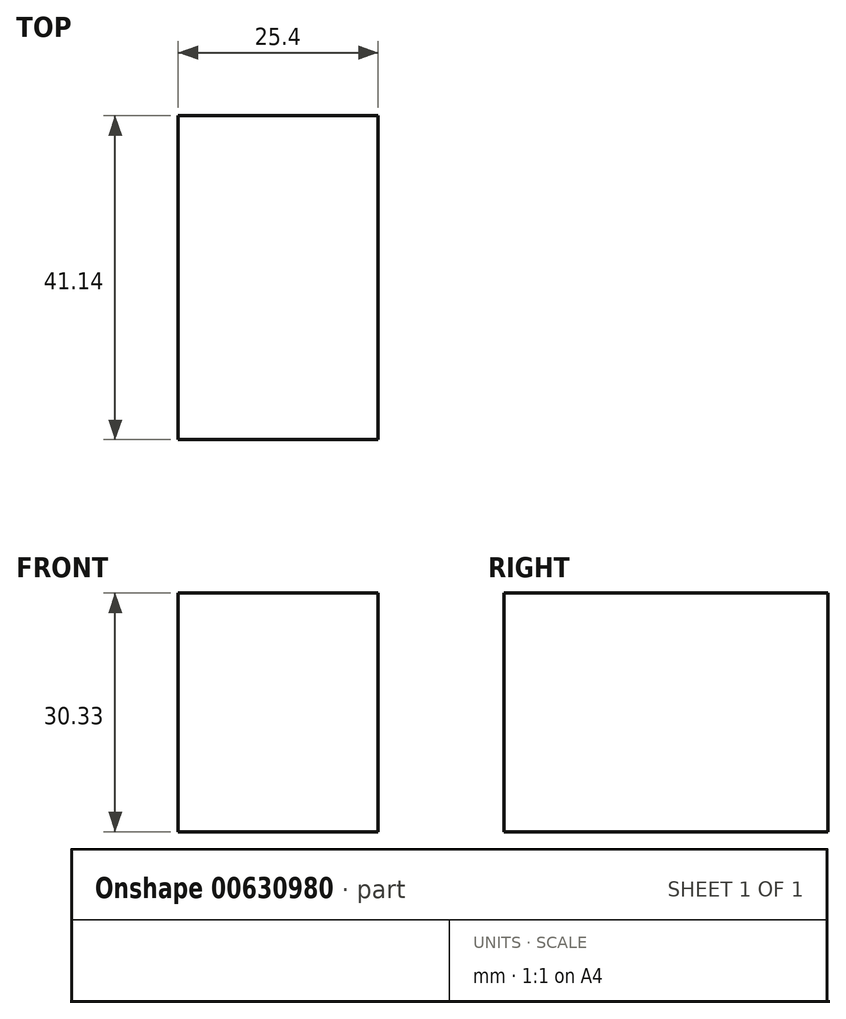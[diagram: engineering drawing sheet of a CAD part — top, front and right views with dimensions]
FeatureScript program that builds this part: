
annotation { "Feature Type Name" : "Feature", "Feature Type Description" : "" }
export const myFeature = defineFeature(function(context is Context, id is Id, definition is map)
    precondition{}
    {
        {
            var Q0;
            Q0=qCreatedBy(makeId("Right.planeOp"),FACE);
            var sketch = newSketch(context, id + "F0", { "sketchPlane" : qUnion([Q0])});
            skLineSegment(sketch, "E0.bottom", {"start": v(-19.35, 15.34) * mm, "end": v(21.79, 15.34) * mm});
            skLineSegment(sketch, "E0.top", {"start": v(-19.35, -15) * mm, "end": v(21.79, -15) * mm});
            skLineSegment(sketch, "E0.left", {"start": v(-19.35, 15.34) * mm, "end": v(-19.35, -15) * mm});
            skLineSegment(sketch, "E0.right", {"start": v(21.79, 15.34) * mm, "end": v(21.79, -15) * mm});
            skSolve(sketch);
        }
        {
            var Q0;
            Q0=makeQuery(id+"F0.imprint","IMPRINT",FACE,{"disambiguationData":[TD([[makeQuery(id+"F0.imprint","IMPRINT",EDGE,{"derivedFrom":sQuery(id+"F0.wireOp",EDGE,"E0.bottom")}),-1.0]])]});
            extrude(context, id + "F1", {"entities" : qUnion([Q0]), "depth" : 25.4 * mm, "offsetDistance" : 25.4 * mm});
        }
    });
